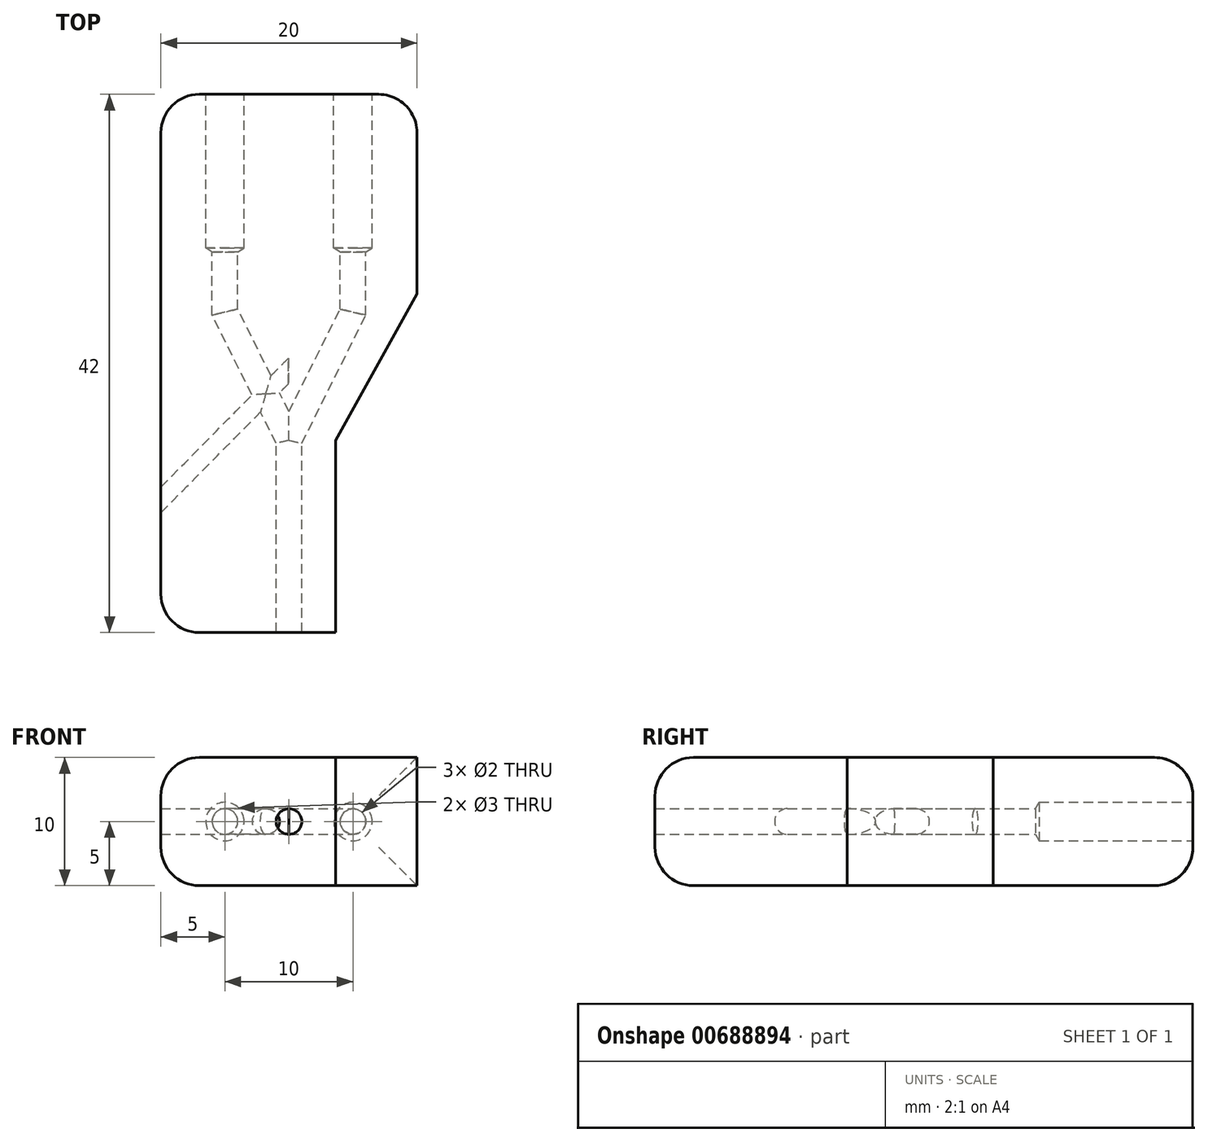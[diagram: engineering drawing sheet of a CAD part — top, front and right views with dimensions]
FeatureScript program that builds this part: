
annotation { "Feature Type Name" : "Feature", "Feature Type Description" : "" }
export const myFeature = defineFeature(function(context is Context, id is Id, definition is map)
    precondition{}
    {
        {
            var Q0;
            Q0=qCreatedBy(makeId("Top.planeOp"),FACE);
            var sketch = newSketch(context, id + "F0", { "sketchPlane" : qUnion([Q0])});
            skLineSegment(sketch, "E0.bottom", {"start": v(0, 27) * mm, "end": v(10, 27) * mm});
            skLineSegment(sketch, "E0.top", {"start": v(0, -15) * mm, "end": v(10, -15) * mm});
            skLineSegment(sketch, "E0.left", {"start": v(0, 27) * mm, "end": v(0, -15) * mm});
            skLineSegment(sketch, "E0.right", {"start": v(10, 27) * mm, "end": v(10, -15) * mm});
            skSolve(sketch);
        }
        {
            var Q0;
            Q0=qSketchRegion(id+"F0",true);
            extrude(context, id + "F1", {"entities" : qUnion([Q0]), "depth" : 5 * mm, "offsetDistance" : 25 * mm});
        }
        {
            var Q0;
            Q0=makeQuery(id+"F1.opExtrude","CAP_FACE",FACE,{"disambiguationData":[OSD([sQuery(id+"F0.wireOp",EDGE,"E0.bottom"),sQuery(id+"F0.wireOp",EDGE,"E0.top"),sQuery(id+"F0.wireOp",EDGE,"E0.left"),sQuery(id+"F0.wireOp",EDGE,"E0.right")])],"isStart":false});
            var sketch = newSketch(context, id + "F2", { "sketchPlane" : qUnion([Q0])});
            skLineSegment(sketch, "E1", {"start": v(5, 27) * mm, "end": v(5, 10) * mm});
            skLineSegment(sketch, "E2", {"start": v(5, 10) * mm, "end": v(0, 0) * mm});
            skLineSegment(sketch, "E3", {"start": v(0, 0) * mm, "end": v(0, -15) * mm});
            skLineSegment(sketch, "E4.MirrorCS", {"start": v(-5, 27) * mm, "end": v(-5, 10) * mm, "construction": true});
            skLineSegment(sketch, "E5.MirrorCS", {"start": v(-5, 10) * mm, "end": v(0, 0) * mm, "construction": true});
            skSolve(sketch);
        }
        {
            var Q0;
            Q0=makeQuery(id+"F1.opExtrude","SWEPT_FACE",FACE,{"disambiguationData":[OSD([sQuery(id+"F0.wireOp",EDGE,"E0.top")])]});
            var sketch = newSketch(context, id + "F3", { "sketchPlane" : qUnion([Q0])});
            skCircle(sketch, "E6", {"center": v(0, 5) * mm, "radius": 1 * mm});
            skSolve(sketch);
        }
        {
            var Q0;
            Q0=qSketchRegion(id+"F3",true);
            var Q1;
            Q1=qConstructionFilter(qBodyType(qCreatedBy(id+"F2",EDGE),BodyType.WIRE),ConstructionObject.NO);
            sweep(context, id + "F4", {"operationType" : NewBodyOperationType.REMOVE, "profiles" : qUnion([Q0]), "path" : qUnion([Q1])});
        }
        {
            var Q0;
            Q0=makeQuery(id+"F1.opExtrude","SWEPT_BODY",BODY,{"disambiguationData":[OSD([sQuery(id+"F0.wireOp",EDGE,"E0.bottom"),sQuery(id+"F0.wireOp",EDGE,"E0.top"),sQuery(id+"F0.wireOp",EDGE,"E0.left"),sQuery(id+"F0.wireOp",EDGE,"E0.right")])]});
            var Q1;
            Q1=makeQuery(id+"F1.opExtrude","SWEPT_FACE",FACE,{"disambiguationData":[OSD([sQuery(id+"F0.wireOp",EDGE,"E0.left")])]});
            mirror(context, id + "F5", {"operationType" : NewBodyOperationType.ADD, "entities" : qUnion([Q0]), "mirrorPlane" : qUnion([Q1])});
        }
        {
            var Q0;
            Q0=makeQuery(id+"F5.opPattern","COPY",FACE,{"derivedFrom":makeQuery(id+"F1.opExtrude","SWEPT_FACE",FACE,{"disambiguationData":[OSD([sQuery(id+"F0.wireOp",EDGE,"E0.right")])]}),"instanceName":"1"});
            var sketch = newSketch(context, id + "F6", { "sketchPlane" : qUnion([Q0])});
            skCircle(sketch, "E7", {"center": v(4.66, 5) * mm, "radius": 1 * mm});
            skSolve(sketch);
        }
        {
            var Q0;
            Q0=makeQuery(id+"F1.opExtrude","SWEPT_BODY",BODY,{"disambiguationData":[OSD([sQuery(id+"F0.wireOp",EDGE,"E0.bottom"),sQuery(id+"F0.wireOp",EDGE,"E0.top"),sQuery(id+"F0.wireOp",EDGE,"E0.left"),sQuery(id+"F0.wireOp",EDGE,"E0.right")])]});
            var Q1;
            {var subQ2=sQuery(id+"F0.wireOp",EDGE,"E0.right");var subQ6=sQuery(id+"F0.wireOp",EDGE,"E0.bottom");var subQ7=makeQuery(id+"F1.opExtrude","SWEPT_FACE",FACE,{"disambiguationData":[OSD([subQ6])]});var subQ9=sQuery(id+"F0.wireOp",EDGE,"E0.top");Q1=makeQuery(id+"FCDVhzvhDTDVJ4q_1.boolean.opBoolean","SPLIT",FACE,{"disambiguationData":[TD([subQ7])],"derivedFrom":makeQuery(id+"F5.opPattern","COPY",FACE,{"derivedFrom":makeQuery(id+"F4.boolean.opBoolean","SPLIT",FACE,{"disambiguationData":[TD([makeQuery(id+"F1.opExtrude","SWEPT_FACE",FACE,{"disambiguationData":[OSD([subQ9])]})])],"derivedFrom":makeQuery(id+"F1.opExtrude","CAP_FACE",FACE,{"disambiguationData":[OSD([subQ6,subQ9,sQuery(id+"F0.wireOp",EDGE,"E0.left"),subQ2])],"isStart":false})}),"instanceName":"1"})});}
            mirror(context, id + "F7", {"operationType" : NewBodyOperationType.ADD, "entities" : qUnion([Q0]), "mirrorPlane" : qUnion([Q1])});
        }
        {
            var Q0;
            {var subQ0=makeQuery(id+"F1.opExtrude","CAP_FACE",FACE,{"disambiguationData":[OSD([sQuery(id+"F0.wireOp",EDGE,"E0.bottom"),sQuery(id+"F0.wireOp",EDGE,"E0.top"),sQuery(id+"F0.wireOp",EDGE,"E0.left"),sQuery(id+"F0.wireOp",EDGE,"E0.right")])],"isStart":true});Q0=makeQuery(id+"F7.opPattern","COPY",FACE,{"derivedFrom":makeQuery(id+"F5.boolean.opBoolean","MERGE",FACE,{"derivedFrom":[subQ0,makeQuery(id+"F5.opPattern","COPY",FACE,{"derivedFrom":subQ0,"instanceName":"1"})]}),"instanceName":"1"});}
            var sketch = newSketch(context, id + "F8", { "sketchPlane" : qUnion([Q0])});
            skLineSegment(sketch, "E8", {"start": v(10, 11.41) * mm, "end": v(3.66, 0) * mm});
            skLineSegment(sketch, "E9", {"start": v(3.66, 0) * mm, "end": v(3.66, -15) * mm});
            skLineSegment(sketch, "E10", {"start": v(3.66, -15) * mm, "end": v(10, -15) * mm});
            skLineSegment(sketch, "E11", {"start": v(10, -15) * mm, "end": v(10, 11.41) * mm});
            skSolve(sketch);
        }
        {
            var Q0;
            Q0=qSketchRegion(id+"F8",true);
            extrude(context, id + "F9", {"entities" : qUnion([Q0]), "operationType" : NewBodyOperationType.REMOVE, "oppositeDirection" : true, "depth" : 10 * mm, "offsetDistance" : 25 * mm});
        }
        {
            var Q0;
            Q0=makeQuery(id+"F9.boolean.opBoolean","COPY",EDGE,{"derivedFrom":makeQuery(id+"F9.opExtrude","CAP_EDGE",EDGE,{"disambiguationData":[OSD([sQuery(id+"F8.wireOp",EDGE,"E9")])],"isStart":true})});
            var Q1;
            Q1=makeQuery(id+"F9.boolean.opBoolean","COPY",EDGE,{"derivedFrom":makeQuery(id+"F9.opExtrude","CAP_EDGE",EDGE,{"disambiguationData":[OSD([sQuery(id+"F8.wireOp",EDGE,"E9")])],"isStart":false})});
            var Q2;
            {var subQ0=makeQuery(id+"F1.opExtrude","CAP_EDGE",EDGE,{"disambiguationData":[OSD([sQuery(id+"F0.wireOp",EDGE,"E0.top")])],"isStart":true});Q2=makeQuery(id+"F7.opPattern","COPY",EDGE,{"derivedFrom":makeQuery(id+"F5.boolean.opBoolean","MERGE",EDGE,{"derivedFrom":[subQ0,makeQuery(id+"F5.opPattern","COPY",EDGE,{"derivedFrom":subQ0,"instanceName":"1"})]}),"instanceName":"1"});}
            var Q3;
            Q3=makeQuery(id+"F9.boolean.opBoolean","COPY",EDGE,{"derivedFrom":makeQuery(id+"F9.opExtrude","SWEPT_EDGE",EDGE,{"disambiguationData":[OSD([sQuery(id+"F0.wireOp",EDGE,"E0.top"),sQuery(id+"F8.wireOp",EDGE,"E9"),sQuery(id+"F8.wireOp",EDGE,"E10")])]})});
            var Q4;
            {var subQ0=makeQuery(id+"F5.opPattern","COPY",EDGE,{"derivedFrom":makeQuery(id+"F1.opExtrude","SWEPT_EDGE",EDGE,{"disambiguationData":[OSD([sQuery(id+"F0.wireOp",EDGE,"E0.top"),sQuery(id+"F0.wireOp",EDGE,"E0.right")])]}),"instanceName":"1"});Q4=makeQuery(id+"F7.boolean.opBoolean","MERGE",EDGE,{"derivedFrom":[subQ0,makeQuery(id+"F7.opPattern","COPY",EDGE,{"derivedFrom":subQ0,"instanceName":"1"})]});}
            var Q5;
            {var subQ0=makeQuery(id+"F1.opExtrude","CAP_EDGE",EDGE,{"disambiguationData":[OSD([sQuery(id+"F0.wireOp",EDGE,"E0.top")])],"isStart":true});Q5=makeQuery(id+"F5.boolean.opBoolean","MERGE",EDGE,{"derivedFrom":[subQ0,makeQuery(id+"F5.opPattern","COPY",EDGE,{"derivedFrom":subQ0,"instanceName":"1"})]});}
            var Q6;
            Q6=makeQuery(id+"F5.opPattern","COPY",EDGE,{"derivedFrom":makeQuery(id+"F1.opExtrude","CAP_EDGE",EDGE,{"disambiguationData":[OSD([sQuery(id+"F0.wireOp",EDGE,"E0.right")])],"isStart":true}),"instanceName":"1"});
            var Q7;
            Q7=makeQuery(id+"F7.opPattern","COPY",EDGE,{"derivedFrom":makeQuery(id+"F5.opPattern","COPY",EDGE,{"derivedFrom":makeQuery(id+"F1.opExtrude","CAP_EDGE",EDGE,{"disambiguationData":[OSD([sQuery(id+"F0.wireOp",EDGE,"E0.right")])],"isStart":true}),"instanceName":"1"}),"instanceName":"1"});
            var Q8;
            Q8=makeQuery(id+"F9.boolean.opBoolean","COPY",EDGE,{"derivedFrom":makeQuery(id+"F9.opExtrude","CAP_EDGE",EDGE,{"disambiguationData":[OSD([sQuery(id+"F8.wireOp",EDGE,"E8")])],"isStart":true})});
            var Q9;
            Q9=makeQuery(id+"F9.boolean.opBoolean","COPY",EDGE,{"derivedFrom":makeQuery(id+"F9.opExtrude","CAP_EDGE",EDGE,{"disambiguationData":[OSD([sQuery(id+"F8.wireOp",EDGE,"E8")])],"isStart":false})});
            var Q10;
            Q10=makeQuery(id+"F9.boolean.opBoolean","COPY",EDGE,{"derivedFrom":makeQuery(id+"F9.opExtrude","SWEPT_EDGE",EDGE,{"disambiguationData":[OSD([sQuery(id+"F0.wireOp",EDGE,"E0.right"),sQuery(id+"F8.wireOp",EDGE,"E8"),sQuery(id+"F8.wireOp",EDGE,"E11")])]})});
            var Q11;
            {var subQ0=makeQuery(id+"F1.opExtrude","CAP_EDGE",EDGE,{"disambiguationData":[OSD([sQuery(id+"F0.wireOp",EDGE,"E0.bottom")])],"isStart":true});Q11=makeQuery(id+"F5.boolean.opBoolean","MERGE",EDGE,{"derivedFrom":[subQ0,makeQuery(id+"F5.opPattern","COPY",EDGE,{"derivedFrom":subQ0,"instanceName":"1"})]});}
            var Q12;
            {var subQ0=makeQuery(id+"F1.opExtrude","CAP_EDGE",EDGE,{"disambiguationData":[OSD([sQuery(id+"F0.wireOp",EDGE,"E0.bottom")])],"isStart":true});Q12=makeQuery(id+"F7.opPattern","COPY",EDGE,{"derivedFrom":makeQuery(id+"F5.boolean.opBoolean","MERGE",EDGE,{"derivedFrom":[subQ0,makeQuery(id+"F5.opPattern","COPY",EDGE,{"derivedFrom":subQ0,"instanceName":"1"})]}),"instanceName":"1"});}
            var Q13;
            {var subQ0=makeQuery(id+"F1.opExtrude","SWEPT_EDGE",EDGE,{"disambiguationData":[OSD([sQuery(id+"F0.wireOp",EDGE,"E0.bottom"),sQuery(id+"F0.wireOp",EDGE,"E0.right")])]});Q13=makeQuery(id+"F7.boolean.opBoolean","MERGE",EDGE,{"derivedFrom":[subQ0,makeQuery(id+"F7.opPattern","COPY",EDGE,{"derivedFrom":subQ0,"instanceName":"1"})]});}
            var Q14;
            {var subQ0=makeQuery(id+"F5.opPattern","COPY",EDGE,{"derivedFrom":makeQuery(id+"F1.opExtrude","SWEPT_EDGE",EDGE,{"disambiguationData":[OSD([sQuery(id+"F0.wireOp",EDGE,"E0.bottom"),sQuery(id+"F0.wireOp",EDGE,"E0.right")])]}),"instanceName":"1"});Q14=makeQuery(id+"F7.boolean.opBoolean","MERGE",EDGE,{"derivedFrom":[subQ0,makeQuery(id+"F7.opPattern","COPY",EDGE,{"derivedFrom":subQ0,"instanceName":"1"})]});}
            fillet(context, id + "F10", {"entities" : qUnion([Q0, Q1, Q2, Q3, Q4, Q5, Q6, Q7, Q8, Q9, Q10, Q11, Q12, Q13, Q14]), "radius" : 3 * mm, "tangentPropagation" : true, "allowEdgeOverflow" : false});
        }
        {
            var Q0;
            {var subQ0=makeQuery(id+"F1.opExtrude","SWEPT_FACE",FACE,{"disambiguationData":[OSD([sQuery(id+"F0.wireOp",EDGE,"E0.bottom")])]});var subQ1=makeQuery(id+"F5.boolean.opBoolean","MERGE",FACE,{"derivedFrom":[subQ0,makeQuery(id+"F5.opPattern","COPY",FACE,{"derivedFrom":subQ0,"instanceName":"1"})]});Q0=makeQuery(id+"F7.boolean.opBoolean","MERGE",FACE,{"derivedFrom":[subQ1,makeQuery(id+"F7.opPattern","COPY",FACE,{"derivedFrom":subQ1,"instanceName":"1"})]});}
            var sketch = newSketch(context, id + "F11", { "sketchPlane" : qUnion([Q0])});
            skPoint(sketch, "E12", {"position": v(-5, 5) * mm});
            skSolve(sketch);
        }
        {
            var Q0;
            Q0=sQuery(id+"F11.wireOp",VERTEX,"E12");
            var Q1;
            Q1=makeQuery(id+"F1.opExtrude","SWEPT_BODY",BODY,{"disambiguationData":[OSD([sQuery(id+"F0.wireOp",EDGE,"E0.bottom"),sQuery(id+"F0.wireOp",EDGE,"E0.top"),sQuery(id+"F0.wireOp",EDGE,"E0.left"),sQuery(id+"F0.wireOp",EDGE,"E0.right")])]});
            hole(context, id + "F12", {"style" : HoleStyle.SIMPLE, "endStyle" : HoleEndStyle.BLIND, "holeDiameter" : 3 * mm, "majorDiameter" : 5 * mm, "holeDepth" : 12 * mm, "isTappedThrough" : true, "tappedDepth" : 12 * mm, "tapClearance" : 3, "locations" : qUnion([Q0]), "scope" : qUnion([Q1])});
        }
        {
            var Q0;
            {var subQ0=makeQuery(id+"F1.opExtrude","SWEPT_FACE",FACE,{"disambiguationData":[OSD([sQuery(id+"F0.wireOp",EDGE,"E0.bottom")])]});var subQ1=makeQuery(id+"F5.boolean.opBoolean","MERGE",FACE,{"derivedFrom":[subQ0,makeQuery(id+"F5.opPattern","COPY",FACE,{"derivedFrom":subQ0,"instanceName":"1"})]});Q0=makeQuery(id+"F7.boolean.opBoolean","MERGE",FACE,{"derivedFrom":[subQ1,makeQuery(id+"F7.opPattern","COPY",FACE,{"derivedFrom":subQ1,"instanceName":"1"})]});}
            var sketch = newSketch(context, id + "F13", { "sketchPlane" : qUnion([Q0])});
            skPoint(sketch, "E13", {"position": v(5, 5) * mm});
            skSolve(sketch);
        }
        {
            var Q0;
            Q0=sQuery(id+"F13.wireOp",VERTEX,"E13");
            var Q1;
            Q1=makeQuery(id+"F1.opExtrude","SWEPT_BODY",BODY,{"disambiguationData":[OSD([sQuery(id+"F0.wireOp",EDGE,"E0.bottom"),sQuery(id+"F0.wireOp",EDGE,"E0.top"),sQuery(id+"F0.wireOp",EDGE,"E0.left"),sQuery(id+"F0.wireOp",EDGE,"E0.right")])]});
            hole(context, id + "F14", {"style" : HoleStyle.SIMPLE, "endStyle" : HoleEndStyle.BLIND, "holeDiameter" : 3 * mm, "majorDiameter" : 5 * mm, "holeDepth" : 12 * mm, "isTappedThrough" : true, "tappedDepth" : 12 * mm, "tapClearance" : 3, "locations" : qUnion([Q0]), "scope" : qUnion([Q1])});
        }
        {
            var Q0;
            Q0=qCreatedBy(makeId("Top.planeOp"),FACE);
            cPlane(context, id + "F15", {"entities" : qUnion([Q0]), "cplaneType" : CPlaneType.OFFSET, "offset" : 5 * mm, "width" : 150 * mm, "height" : 150 * mm});
        }
        {
            var Q0;
            Q0=qCreatedBy(id+"F15.planeOp",FACE);
            var sketch = newSketch(context, id + "F16", { "sketchPlane" : qUnion([Q0])});
            skPoint(sketch, "E14", {"position": v(-9.95, -4.7) * mm});
            skLineSegment(sketch, "E15", {"start": v(-9.95, -4.7) * mm, "end": v(0, 5.36) * mm});
            skSolve(sketch);
        }
        {
            var Q0;
            {var subQ0=sQuery(id+"F6.wireOp",EDGE,"E7");var subQ1=makeQuery(id+"F5.opPattern","COPY",EDGE,{"derivedFrom":makeQuery(id+"F1.opExtrude","CAP_EDGE",EDGE,{"disambiguationData":[OSD([sQuery(id+"F0.wireOp",EDGE,"E0.right")])],"isStart":false}),"instanceName":"1"});var subQ2=makeQuery(id+"F6.imprint","INTERSECT",VERTEX,{"disambiguationData":[OD(0.0)],"derivedFrom":[subQ1,subQ0]});Q0=makeQuery(id+"F6.imprint","IMPRINT",FACE,{"disambiguationData":[TD([[makeQuery(id+"F6.imprint","IMPRINT",EDGE,{"disambiguationData":[TD([[subQ2,1.0]])],"derivedFrom":subQ0}),1.0]])]});}
            var Q1;
            {var subQ0=sQuery(id+"F6.wireOp",EDGE,"E7");var subQ1=makeQuery(id+"F5.opPattern","COPY",EDGE,{"derivedFrom":makeQuery(id+"F1.opExtrude","CAP_EDGE",EDGE,{"disambiguationData":[OSD([sQuery(id+"F0.wireOp",EDGE,"E0.right")])],"isStart":false}),"instanceName":"1"});var subQ2=makeQuery(id+"F6.imprint","INTERSECT",VERTEX,{"disambiguationData":[OD(0.0)],"derivedFrom":[subQ1,subQ0]});Q1=makeQuery(id+"F6.imprint","IMPRINT",FACE,{"disambiguationData":[TD([[makeQuery(id+"F6.imprint","IMPRINT",EDGE,{"disambiguationData":[TD([[subQ2,-1.0]])],"derivedFrom":subQ0}),1.0]])]});}
            var Q2;
            Q2=sQuery(id+"F16.wireOp",EDGE,"E15");
            sweep(context, id + "F17", {"operationType" : NewBodyOperationType.REMOVE, "profiles" : qUnion([Q0, Q1]), "path" : qUnion([Q2])});
        }
    });
